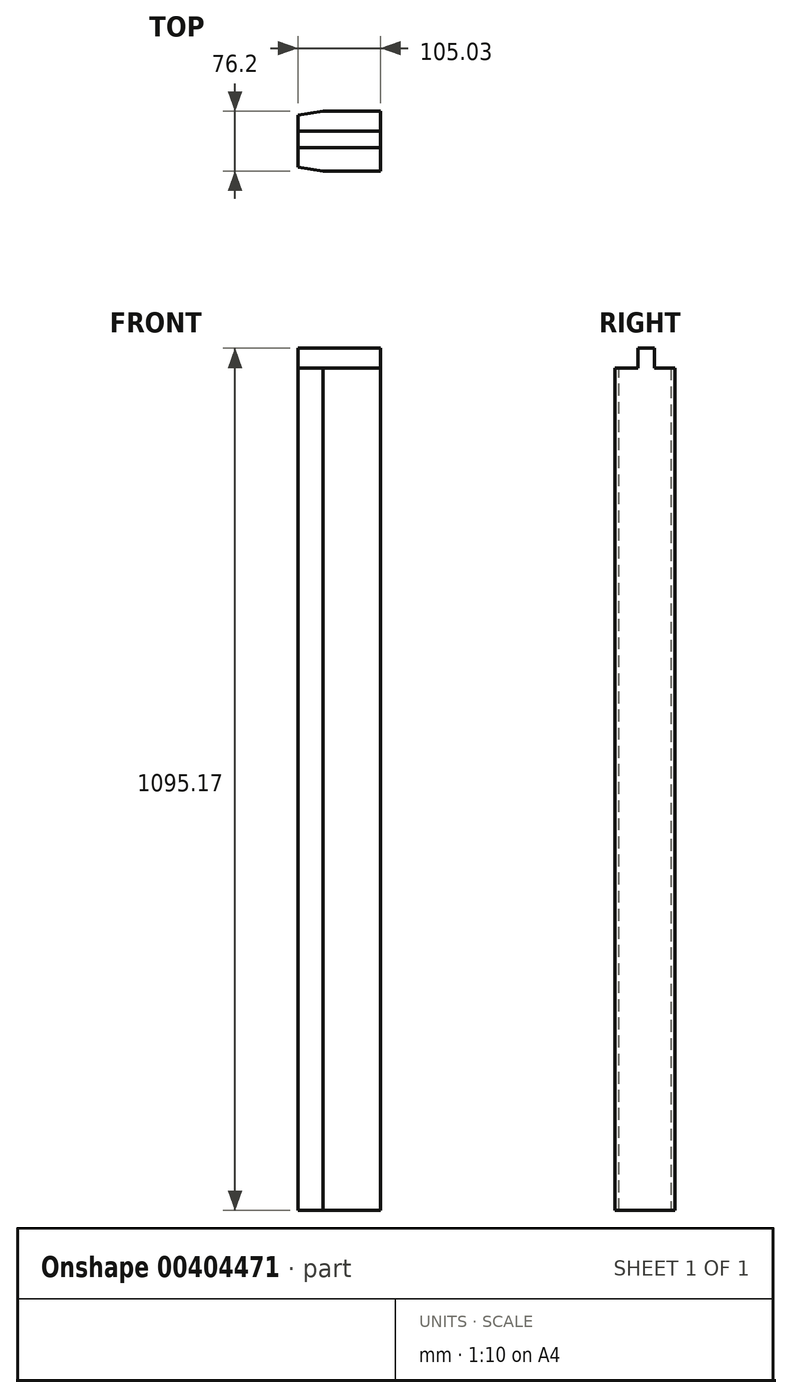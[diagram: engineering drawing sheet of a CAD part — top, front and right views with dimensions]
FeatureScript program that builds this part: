
annotation { "Feature Type Name" : "Feature", "Feature Type Description" : "" }
export const myFeature = defineFeature(function(context is Context, id is Id, definition is map)
    precondition{}
    {
        {
            var Q0;
            Q0=qCreatedBy(makeId("Front.planeOp"),FACE);
            var sketch = newSketch(context, id + "F0", { "sketchPlane" : qUnion([Q0])});
            skLineSegment(sketch, "E0.bottom", {"start": v(-46.93, 38.15) * mm, "end": v(58.1, 38.15) * mm});
            skLineSegment(sketch, "E0.top", {"start": v(-46.93, -41.02) * mm, "end": v(58.1, -41.02) * mm});
            skLineSegment(sketch, "E0.left", {"start": v(-46.93, 38.15) * mm, "end": v(-46.93, -41.02) * mm});
            skLineSegment(sketch, "E0.right", {"start": v(58.1, 38.15) * mm, "end": v(58.1, -41.02) * mm});
            skSolve(sketch);
        }
        {
            var Q0;
            Q0 = qSketchRegion(id + "F0", true);
            extrude(context, id + "F1", {"entities" : qUnion([Q0]), "depth" : 76.2 * mm});
        }
        {
            var Q0;
            Q0=makeQuery(id+"F1.opExtrude","SWEPT_FACE",FACE,{"disambiguationData":[OSD([sQuery(id+"F0.wireOp",EDGE,"E0.bottom")])]});
            extrude(context, id + "F2", {"entities" : qUnion([Q0]), "operationType" : NewBodyOperationType.ADD, "depth" : 990.6 * mm});
        }
        {
            var Q0;
            Q0=makeQuery(id+"F2.opExtrude","CAP_FACE",FACE,{"disambiguationData":[OSD([sQuery(id+"F0.wireOp",EDGE,"E0.bottom")])],"isStart":false});
            var sketch = newSketch(context, id + "F3", { "sketchPlane" : qUnion([Q0])});
            skLineSegment(sketch, "E1.bottom", {"start": v(-46.93, -25.55) * mm, "end": v(58.1, -25.55) * mm});
            skLineSegment(sketch, "E1.top", {"start": v(-46.93, -46.49) * mm, "end": v(58.1, -46.49) * mm});
            skLineSegment(sketch, "E1.left", {"start": v(-46.93, -25.55) * mm, "end": v(-46.93, -46.49) * mm});
            skLineSegment(sketch, "E1.right", {"start": v(58.1, -25.55) * mm, "end": v(58.1, -46.49) * mm});
            skSolve(sketch);
        }
        {
            var Q0;
            Q0 = qSketchRegion(id + "F3", true);
            var Q1;
            Q1=makeQuery(id+"F3.imprint","IMPRINT",FACE,{"disambiguationData":[TD([[makeQuery(id+"F3.imprint","IMPRINT",EDGE,{"derivedFrom":sQuery(id+"F3.wireOp",EDGE,"E1.bottom")}),-1.0]])]});
            extrude(context, id + "F4", {"entities" : qUnion([Q0, Q1]), "operationType" : NewBodyOperationType.ADD, "depth" : 25.4 * mm});
        }
        {
            var Q0;
            {var subQ0=sQuery(id+"F0.wireOp",EDGE,"E0.left");var subQ1=sQuery(id+"F0.wireOp",EDGE,"E0.bottom");Q0=makeQuery(id+"F2.boolean.opBoolean","MERGE",EDGE,{"derivedFrom":[makeQuery(id+"F1.opExtrude","CAP_EDGE",EDGE,{"disambiguationData":[OSD([subQ0])],"isStart":false}),makeQuery(id+"F2.opExtrude","SWEPT_EDGE",EDGE,{"disambiguationData":[OSD([subQ1,subQ0]),TDD([makeQuery(id+"F1.opExtrude","CAP_VERTEX",VERTEX,{"disambiguationData":[OSD([subQ1,subQ0])],"isStart":false})])]})]});}
            chamfer(context, id + "F5", {"entities" : qUnion([Q0]), "chamferType" : ChamferType.OFFSET_ANGLE, "width" : 31.75 * mm, "oppositeDirection" : false, "angle" : 9 * degree, "tangentPropagation" : true});
        }
        {
            var Q0;
            {var subQ0=sQuery(id+"F0.wireOp",EDGE,"E0.left");var subQ1=sQuery(id+"F0.wireOp",EDGE,"E0.bottom");Q0=makeQuery(id+"F2.boolean.opBoolean","MERGE",EDGE,{"derivedFrom":[makeQuery(id+"F1.opExtrude","CAP_EDGE",EDGE,{"disambiguationData":[OSD([subQ0])],"isStart":true}),makeQuery(id+"F2.opExtrude","SWEPT_EDGE",EDGE,{"disambiguationData":[OSD([subQ1,subQ0]),TDD([makeQuery(id+"F1.opExtrude","CAP_VERTEX",VERTEX,{"disambiguationData":[OSD([subQ1,subQ0])],"isStart":true})])]})]});}
            chamfer(context, id + "F6", {"entities" : qUnion([Q0]), "chamferType" : ChamferType.OFFSET_ANGLE, "width" : 31.75 * mm, "oppositeDirection" : true, "angle" : 9 * degree, "tangentPropagation" : true});
        }
        {
            var Q0;
            {var subQ0=sQuery(id+"F0.wireOp",EDGE,"E0.right");Q0=makeQuery(id+"F4.boolean.opBoolean","MERGE",FACE,{"derivedFrom":[makeQuery(id+"F2.boolean.opBoolean","MERGE",FACE,{"derivedFrom":[makeQuery(id+"F1.opExtrude","SWEPT_FACE",FACE,{"disambiguationData":[OSD([subQ0])]}),makeQuery(id+"F2.opExtrude","SWEPT_FACE",FACE,{"disambiguationData":[OSD([sQuery(id+"F0.wireOp",EDGE,"E0.bottom"),subQ0])]})]}),makeQuery(id+"F4.opExtrude","SWEPT_FACE",FACE,{"disambiguationData":[OSD([sQuery(id+"F3.wireOp",EDGE,"E1.right")])]})]});}
            var sketch = newSketch(context, id + "F7", { "sketchPlane" : qUnion([Q0])});
            skLineSegment(sketch, "E2", {"start": v(0, 1028.75) * mm, "end": v(-12.78, 1028.75) * mm});
            skSolve(sketch);
        }
        {
            var Q0;
            {var subQ3=sQuery(id+"F7.wireOp",EDGE,"E2");Q0=makeQuery(id+"F7.imprint","IMPRINT",FACE,{"disambiguationData":[TD([[makeQuery(id+"F7.imprint","IMPRINT",EDGE,{"derivedFrom":subQ3}),-1.0]])]});}
            var sketch = newSketch(context, id + "F8", { "sketchPlane" : qUnion([Q0])});
            skLineSegment(sketch, "E3.bottom", {"start": v(0, 1028.72) * mm, "end": v(-13.02, 1028.72) * mm});
            skLineSegment(sketch, "E3.top", {"start": v(0, -125.81) * mm, "end": v(-13.02, -125.81) * mm});
            skLineSegment(sketch, "E3.left", {"start": v(0, 1028.72) * mm, "end": v(0, -125.81) * mm});
            skLineSegment(sketch, "E3.right", {"start": v(-13.02, 1028.72) * mm, "end": v(-13.02, -125.81) * mm});
            skSolve(sketch);
        }
        {
            var Q0;
            Q0=sQuery(id+"F8.wireOp",EDGE,"E3.left");
            var Q1;
            Q1=sQuery(id+"F8.wireOp",EDGE,"E3.right");
            extrude(context, id + "F9", {"bodyType" : ToolBodyType.SURFACE, "surfaceEntities" : qUnion([Q0, Q1]), "oppositeDirection" : true, "depth" : 38.1 * mm});
        }
    });
